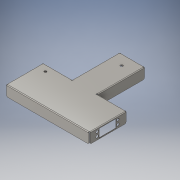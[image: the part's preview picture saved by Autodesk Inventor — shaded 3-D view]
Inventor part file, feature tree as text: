
AUTODESK INVENTOR PART (.ipt)
format: ipt  version: 2016 (Build 200138000, 138)  size: 463,872 bytes
history: native  units: in
note: dims shown in document units (in); Inventor stores cm internally (conversion verified against a paired STEP export)
features: other x12, sketch x10, sheet_metal_op x6, fillet x3
ambient origin geometry x8: Origin, YZ Plane, XZ Plane, XY Plane, X Axis, Y Axis, Z Axis, Center Point
bodies: Solid1 (feature_tree)
feature tree (31):
  sheet_metal_op  "Face1"
  sheet_metal_op  "Face2"
  sheet_metal_op  "Flange1"
  sketch  "Sketch9"  dims[d12=3.4374in]
  sketch  "Sketch18"  dims[d14=0.034in]
  sketch  "Sketch21"  dims[d16=0.068in]
  sketch  "Sketch22"  dims[d17=0.034in]
  fillet  "Fillet1"  Radius=2.3in
  fillet  "Fillet2"  Radius=8.0in
  fillet  "Fillet3"  Radius=0.034in
  sketch  "Sketch2"  dims[d9=3.4374in]
  other  "Plate1"
  sketch  "Sketch4"  dims[d10=2.7993in]
  other  "Plate2"
  sheet_metal_op  "Bend1"
  sketch  "Sketch5"  dims[d11=2.799in]
  other  "Plate3"
  sheet_metal_op  "Bend2"
  sheet_metal_op  "Corner1"
  sketch  "Sketch13"  dims[d13=0.034in]
  sketch  "Sketch20"  dims[d15=0.017in]
  sketch  "Sketch23"  dims[d18=0.034in d19=0.017in d20=0.068in d21=0.034in d22=1.0in d23=90.0deg d24=0.034in d25=0.136in d26=0.034in d27=0.034in d39=0.25in d40=0.034in d41=0.0in d42=0.8in d53=0.917in d55=0.034in d56=0.0in d57=0.917in d64=45.0deg d65=0.034in d66=0.0in d67=0.917in d71=1.625in d72=12.0in d73=0.0in d74=12.0in d75=0.0in d76=0.034in d77=0.0in d78=0.034in d79=0.0in d80=0.2307in d81=0.034in d82=0.0in d83=0.125in d84=0.125in d85=0.125in]
  other  "Cut5"
  other  "Cut7"
  other  "Cut10"
  other  "Cut12"
  other  "Cut13"
  other  "Cut14"
  other  "Cut15"
  other  "Cut16"
  other  "Definition1"
